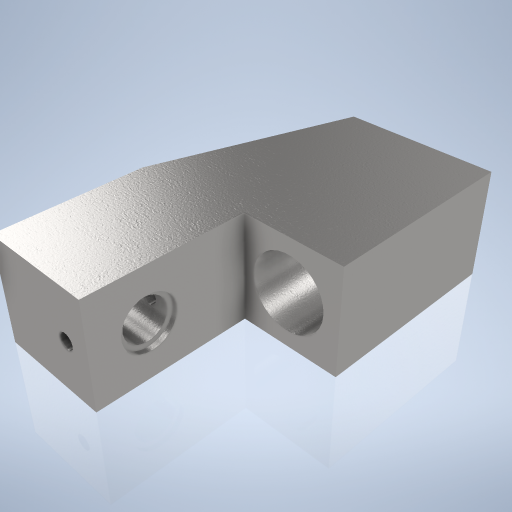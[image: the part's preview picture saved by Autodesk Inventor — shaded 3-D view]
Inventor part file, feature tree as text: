
AUTODESK INVENTOR PART (.ipt)
format: ipt  version: 2024.2 (Build 282272000, 272)  size: 346,624 bytes
history: native  units: mm
features: sketch x5, hole x4, plane x2, extrude x1, mirror x1, projected_geometry x1
ambient origin geometry x8: Origin, YZ Plane, XZ Plane, XY Plane, X Axis, Y Axis, Z Axis, Center Point
bodies: Volumenkörper1 (feature_tree)
feature tree (14):
  extrude  "Extrusion1"  Depth=21.0mm
  hole  "Bohrung2"  [1 undecoded]
  hole  "Bohrung3"  [1 undecoded]
  hole  "Bohrung4"  [1 undecoded]
  plane  "Arbeitsebene1"
  hole  "Bohrung7"  [1 undecoded]
  plane  "Arbeitsebene2"
  mirror  "Spiegeln2"
  sketch  "Skizze1"  dims[d0=65.0mm d1=21.0mm]
  sketch  "Skizze3"  dims[d2=29.0mm d3=38.0mm]
  sketch  "Skizze4"  dims[d4=28.0mm d5=12.0mm]
  sketch  "Skizze5"  dims[d6=20.0mm d7=0.0mm d16=10.0mm]
  sketch  "Skizze8"  dims[d17=14.0mm d18=6.0mm d19=4.0mm d20=2.0mm d21=90.0deg d22=8.0mm d23=20.594885mm d24=4.0mm d25=3.0mm d26=6.0mm d27=4.0mm d28=30.0mm d29=90.0deg d30=8.0mm d31=0.0mm d32=10.5mm d33=8.0mm d34=6.0mm d35=10.0mm d36=1.0mm d37=90.0deg d38=8.0mm d39=20.594885mm d49=12.0mm d57=14.0mm d58=2.459mm d59=6.0mm d60=4.0mm d61=2.0mm d62=90.0deg d63=9.0mm d64=20.594885mm d65=26.5mm]
  projected_geometry  "Projizierte Kontur1"
note: 4 required parameter values undecoded (feature->parameter linkage not recoverable at this tier; creation-order binding heuristic only, values carry confidence <= 0.55)
